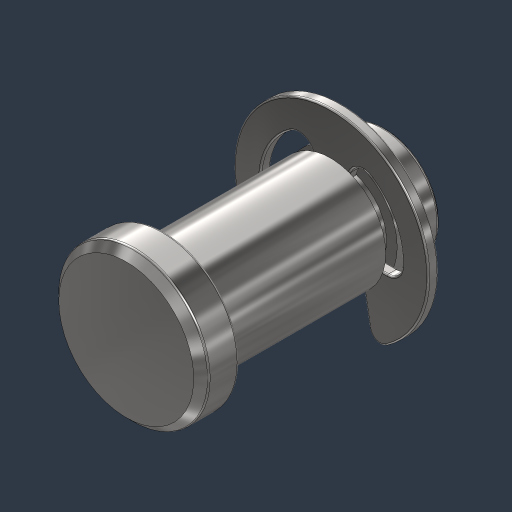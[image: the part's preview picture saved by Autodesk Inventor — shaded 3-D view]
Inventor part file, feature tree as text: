
AUTODESK INVENTOR PART (.ipt)
format: ipt  version: 2024.3 (Build 283343000, 343)  size: 238,080 bytes
history: native  units: mm (DEFAULTED — no unit token found)
features: fillet x2
ambient origin geometry x8: Origin, YZ Plane, XZ Plane, XY Plane, X Axis, Y Axis, Z Axis, Center Point
bodies: Solid1 (feature_tree), Solid2 (feature_tree)
feature tree (2):
  fillet  "Fillet4"  [1 undecoded]
  fillet  "Fillet2"  [1 undecoded]
note: 2 required parameter values undecoded (feature->parameter linkage not recoverable at this tier; creation-order binding heuristic only, values carry confidence <= 0.55)
